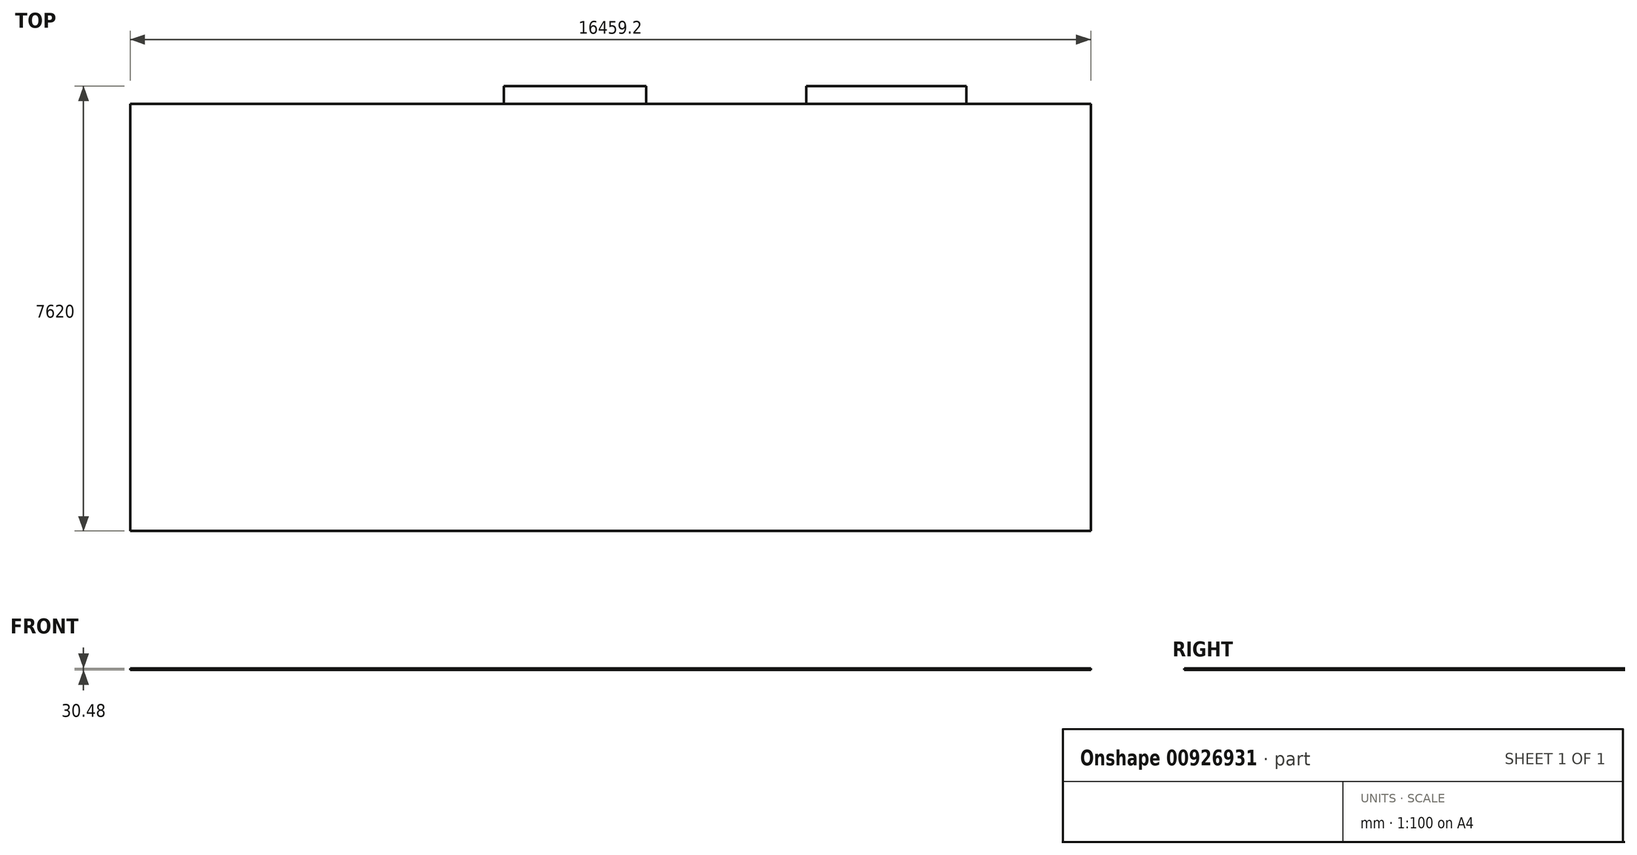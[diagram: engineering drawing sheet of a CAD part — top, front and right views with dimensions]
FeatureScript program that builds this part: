
annotation { "Feature Type Name" : "Feature", "Feature Type Description" : "" }
export const myFeature = defineFeature(function(context is Context, id is Id, definition is map)
    precondition{}
    {
        {
            var Q0;
            Q0=qCreatedBy(makeId("Top.planeOp"),FACE);
            var sketch = newSketch(context, id + "F0", { "sketchPlane" : qUnion([Q0])});
            skLineSegment(sketch, "E0.bottom", {"start": v(8229.6, -3657.6) * mm, "end": v(-8229.6, -3657.6) * mm});
            skLineSegment(sketch, "E0.top", {"start": v(8229.6, 3657.6) * mm, "end": v(-8229.6, 3657.6) * mm});
            skLineSegment(sketch, "E0.left", {"start": v(8229.6, -3657.6) * mm, "end": v(8229.6, 3657.6) * mm});
            skLineSegment(sketch, "E0.right", {"start": v(-8229.6, -3657.6) * mm, "end": v(-8229.6, 3657.6) * mm});
            skPoint(sketch, "E0.middle", {"position": v(0, 0) * mm});
            skSolve(sketch);
        }
        {
            var Q0;
            Q0=makeQuery(id+"F0.imprint","IMPRINT",FACE,{"disambiguationData":[TD([[makeQuery(id+"F0.imprint","IMPRINT",EDGE,{"derivedFrom":sQuery(id+"F0.wireOp",EDGE,"E0.bottom")}),-1.0]])]});
            extrude(context, id + "F1", {"entities" : qUnion([Q0]), "depth" : 30.48 * mm, "offsetDistance" : 30.48 * mm});
        }
        {
            var Q0;
            Q0=makeQuery(id+"F1.opExtrude","CAP_FACE",FACE,{"disambiguationData":[OSD([sQuery(id+"F0.wireOp",EDGE,"E0.bottom"),sQuery(id+"F0.wireOp",EDGE,"E0.top"),sQuery(id+"F0.wireOp",EDGE,"E0.left"),sQuery(id+"F0.wireOp",EDGE,"E0.right")])],"isStart":false});
            var sketch = newSketch(context, id + "F2", { "sketchPlane" : qUnion([Q0])});
            skLineSegment(sketch, "E1", {"start": v(8229.6, 3657.6) * mm, "end": v(6096, 3657.6) * mm});
            skLineSegment(sketch, "E2", {"start": v(6096, 3657.6) * mm, "end": v(609.6, 3657.6) * mm});
            skLineSegment(sketch, "E3", {"start": v(609.6, 3657.6) * mm, "end": v(-1828.8, 3657.6) * mm});
            skLineSegment(sketch, "E4", {"start": v(-1828.8, 3657.6) * mm, "end": v(-1828.8, 3962.4) * mm});
            skLineSegment(sketch, "E5", {"start": v(-1828.8, 3962.4) * mm, "end": v(609.6, 3962.4) * mm});
            skLineSegment(sketch, "E6", {"start": v(609.6, 3962.4) * mm, "end": v(609.6, 3657.6) * mm});
            skLineSegment(sketch, "E7", {"start": v(6096, 3657.6) * mm, "end": v(6096, 3962.4) * mm});
            skLineSegment(sketch, "E8", {"start": v(6096, 3962.4) * mm, "end": v(3352.8, 3962.4) * mm});
            skPoint(sketch, "E8.endSnap0", {"position": v(3352.8, 3657.6) * mm});
            skLineSegment(sketch, "E9", {"start": v(3352.8, 3962.4) * mm, "end": v(3352.8, 3657.6) * mm});
            skSolve(sketch);
        }
        {
            var Q0;
            Q0 = qSketchRegion(id + "F2", true);
            extrude(context, id + "F3", {"entities" : qUnion([Q0]), "oppositeDirection" : true, "depth" : 30.48 * mm, "offsetDistance" : 30.48 * mm});
        }
    });
